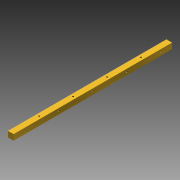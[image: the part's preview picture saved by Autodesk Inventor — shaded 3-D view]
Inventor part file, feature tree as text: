
AUTODESK INVENTOR PART (.ipt)
format: ipt  version: 2016 (Build 200138000, 138)  size: 107,008 bytes
history: native  units: in
note: dims shown in document units (in); Inventor stores cm internally (conversion verified against a paired STEP export)
features: sketch x3, hole x2, pattern_linear x2, extrude x1
ambient origin geometry x8: Origin, YZ Plane, XZ Plane, XY Plane, X Axis, Y Axis, Z Axis, Center Point
bodies: Solid1 (feature_tree)
feature tree (8):
  extrude  "Extrusion1"  Depth=0.25in
  hole  "Hole1"  [1 undecoded]
  pattern_linear  "Rectangular Pattern1"  Count1=5 Spacing1=1.5in
  pattern_linear  "Rectangular Pattern2"  Spacing1=0.75in  [1 undecoded]
  sketch  "Sketch1"  dims[d0=0.25in d2=0.25in]
  sketch  "Sketch2"  dims[d3=7.0in d4=0.0in d5=0.125in]
  sketch  "Sketch3"  dims[d6=0.5in d7=0.067in d8=0.75in d9=0.375in d10=0.25in d11=0.5635in d12=1.0in d13=0.8108in d21=1.9685in d23=1.5in d24=0.75in d27=0.8108in d28=0.5635in d29=0.25in d30=0.375in d31=1.0in d32=0.067in d33=1.25in d34=1.5748in d36=1.5in d37=0.125in]
  hole  "Hole2"  [1 undecoded]
note: 3 required parameter values undecoded (feature->parameter linkage not recoverable at this tier; creation-order binding heuristic only, values carry confidence <= 0.55)
